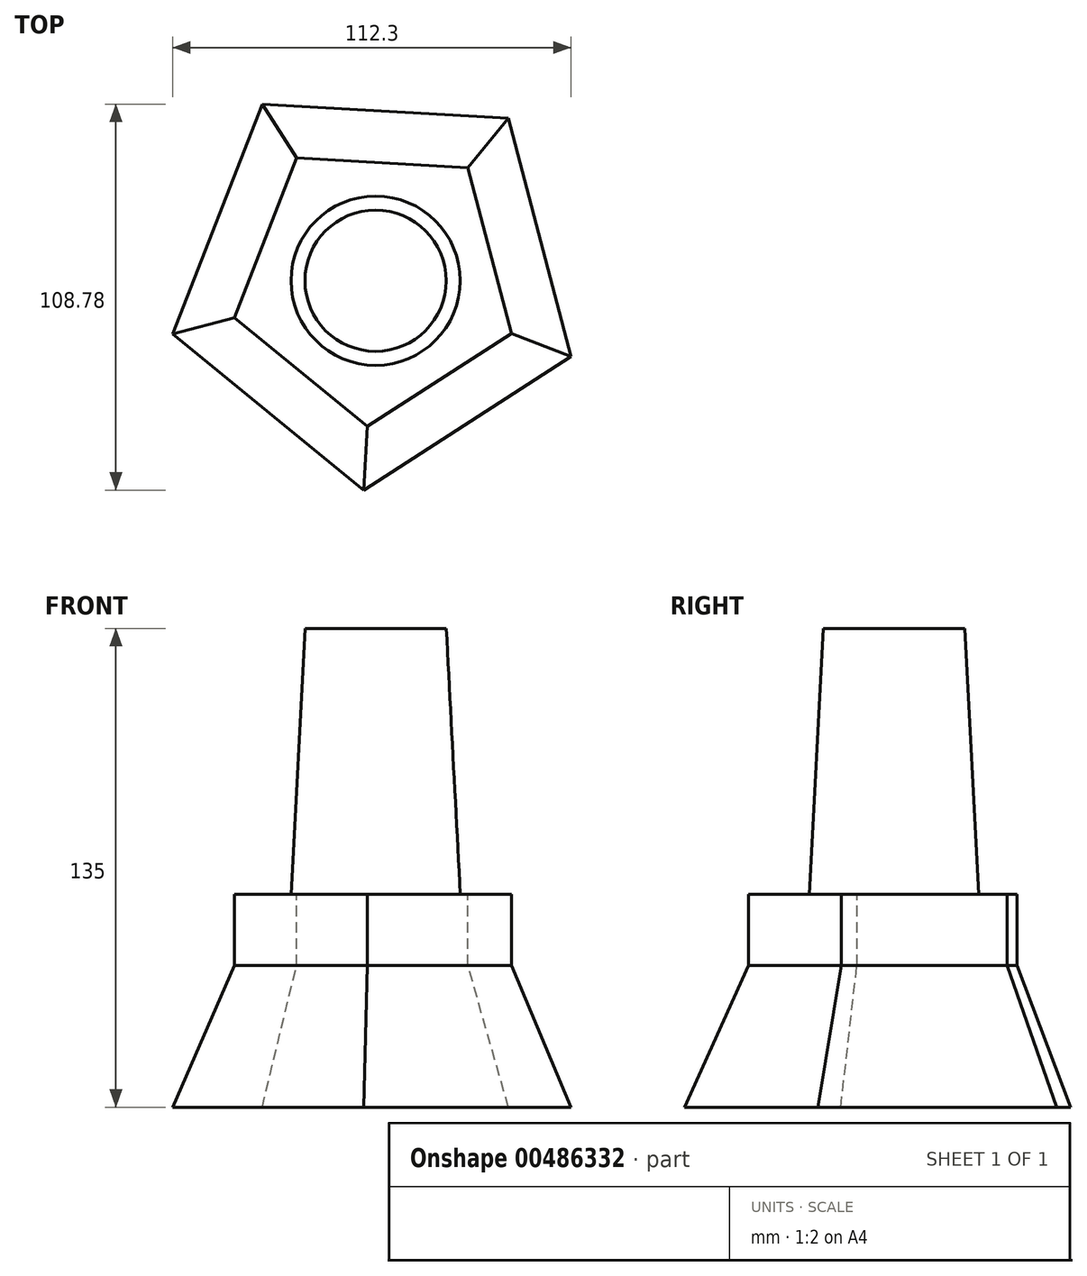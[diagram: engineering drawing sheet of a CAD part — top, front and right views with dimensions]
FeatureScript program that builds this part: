
annotation { "Feature Type Name" : "Feature", "Feature Type Description" : "" }
export const myFeature = defineFeature(function(context is Context, id is Id, definition is map)
    precondition{}
    {
        {
            var Q0;
            Q0=qCreatedBy(makeId("Top.planeOp"),FACE);
            var sketch = newSketch(context, id + "F0", { "sketchPlane" : qUnion([Q0])});
            skCircle(sketch, "E0.cCircle", {"center": v(0, 0) * mm, "radius": 33.28 * mm, "construction": true});
            skLineSegment(sketch, "E0.0", {"start": v(38.34, -14.91) * mm, "end": v(-2.33, -41.07) * mm});
            skLineSegment(sketch, "E0.1", {"start": v(-2.33, -41.07) * mm, "end": v(-39.78, -10.47) * mm});
            skLineSegment(sketch, "E0.2", {"start": v(-39.78, -10.47) * mm, "end": v(-22.26, 34.6) * mm});
            skLineSegment(sketch, "E0.3", {"start": v(-22.26, 34.6) * mm, "end": v(26.03, 31.86) * mm});
            skLineSegment(sketch, "E0.4", {"start": v(26.03, 31.86) * mm, "end": v(38.34, -14.91) * mm});
            skPoint(sketch, "E0.0.midPoint", {"position": v(18, -28) * mm});
            skSolve(sketch);
        }
        {
            var Q0;
            Q0 = qSketchRegion(id + "F0", true);
            extrude(context, id + "F1", {"entities" : qUnion([Q0]), "oppositeDirection" : true, "depth" : 40 * mm, "hasDraft" : true, "draftAngle" : 20 * degree, "hasSecondDirection" : true, "secondDirectionOppositeDirection" : false, "secondDirectionDepth" : 20 * mm});
        }
        {
            var Q0;
            Q0=qCreatedBy(makeId("Top.planeOp"),FACE);
            var sketch = newSketch(context, id + "F2", { "sketchPlane" : qUnion([Q0])});
            skCircle(sketch, "E1", {"center": v(0, 0) * mm, "radius": 24.9 * mm});
            skSolve(sketch);
        }
        {
            var Q0;
            Q0 = qSketchRegion(id + "F2", true);
            extrude(context, id + "F3", {"entities" : qUnion([Q0]), "operationType" : NewBodyOperationType.ADD, "depth" : 95 * mm, "hasDraft" : true, "draftAngle" : 3 * degree, "draftPullDirection" : true});
        }
    });
